# Revit family: Sink-Vessel-Lavatory-KOHLER-PARLIAMENT-K-99182T
name_source: partatom
category: Plumbing Fixtures
revit_build: Autodesk Revit 2017 (Build: 20160225_1515(x64)
units: mm (PartAtom-declared; Revit-internal decimal feet)

## family parameters
Cut with Voids When Loaded = No
Host = Face
OmniClass Number = 23.31.13.00
OmniClass Title = Sinks
Part Type = Normal
Room Calculation Point = No
Round Connector Dimension = Use Diameter
Shared = No

## types (3) — shared parameters
ADA Compliant = No
Assembly Code = D2010400
CW Connection = No
Cold Water Inlet = Cold Water Inlet
Date Modified = 03/24/2021
Default Elevation = 36"
Drain Included = No
Finish = Kohler-Vitreous_China-0-White
HW Connection = No
Height = 7 9/16"
Hot Water Inlet = Hot Water Inlet
Length = 18 13/16"
Manufacturer = KOHLER Co.
Master Format 2014 = 22 41 16
Master Format 2014 Name = Residential Lavatories and Sinks
Material = Vitreous China
Product Name = PARLIAMENT
URL = http://www.kohler.com.cn
Vent Connection = No
Waste Connection = Yes
Waste Water Outlet = Waste Water Outlet
WaterSense Certified = No
Width = 23 15/16"

## per-type parameters (varying)
| type | 4 Inch Faucet Hole Spacing | 8 Inch Faucet Hole Spacing | Description | Faucet Hole Spacing | Model | Product Documentation Link | Product Page URL | Single Faucet Hole | Type |
| Single Faucet Hole, 0-White | No | No | VESSEL 24 INCH SINGLE HOLE | 0" | K-99182T-1-0 | https://files.kohler.com.cn | https://www.kohler.com.cn | Yes | 1 |
| 4 Inch Faucet Hole, 0-White | Yes | No | VESSEL 24 INCH, 4 INCH HOLE | 4" | K-99182T-4-0 |  |  | No | 2 |
| 8 Inch Faucet Hole, 0-White | No | Yes | VESSEL 24 INCH, 8 INCH HOLE | 8" | K-99182T-8-0 | https://files.kohler.com.cn | https://www.kohler.com.cn | No | 3 |

## geometry (parser evidence)
native form markers: Sweep x5
no freeform markers — native parametric forms only
